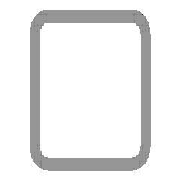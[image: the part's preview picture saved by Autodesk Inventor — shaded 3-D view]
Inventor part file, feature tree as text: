
AUTODESK INVENTOR PART (.ipt)
format: ipt  version: 2025 (Build 290162010, 162A)  size: 142,848 bytes
history: native  units: mm (DEFAULTED — no unit token found)
features: other x4, sketch x1, plane x1
ambient origin geometry x8: Origin, YZ Plane, XZ Plane, XY Plane, X Axis, Y Axis, Z Axis, Center Point
bodies: Solid1 (feature_tree), Body (feature_tree)
feature tree (6):
  parser-record x1  (decoder bookkeeping rows leaked as tree rows — omitted from the tree; the rows remain in map.json)
  other  "Driven Length"
  other  "Start Plane"
  other  "End Plane"
  sketch  "Sketch3"  dims[d3=635.0mm d4=0.0mm d7=4.0mm d9=40.0mm d11=40.0mm d12=2.0mm d13=50.0mm d14=685.0mm d15=20.0mm d16=20.0mm d17=90.0deg d18=635.0mm]
  plane  "Work Plane3"
